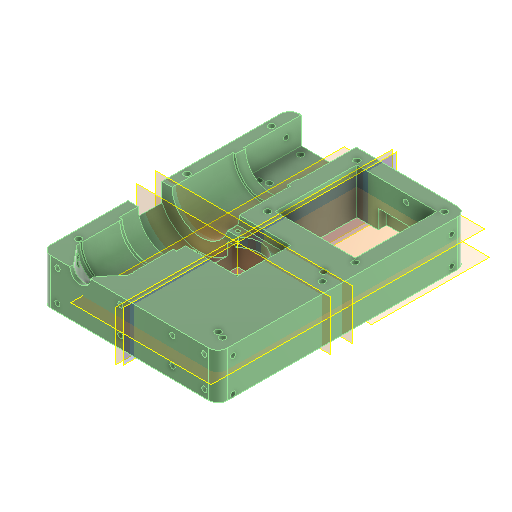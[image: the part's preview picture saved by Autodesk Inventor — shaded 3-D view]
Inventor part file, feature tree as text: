
AUTODESK INVENTOR PART (.ipt)
format: ipt  version: 2024.1 (Build 281209000, 209)  size: 665,600 bytes
history: native  units: mm
features: reference x15, sketch x10, plane x7, other x6, projected_geometry x6, extrude x5, hole x4, mirror x2, revolve x1, fillet x1
ambient origin geometry x8: Origin, YZ Plane, XZ Plane, XY Plane, X Axis, Y Axis, Z Axis, Center Point
bodies: Volumenkörper1 (feature_tree)
feature tree (57):
  plane  "Arbeitsebene1"
  plane  "Arbeitsebene2"
  extrude  "Extrusion1"  Depth=2.8mm
  revolve  "Umdrehung1"
  extrude  "Extrusion4"  Depth=2.8mm
  hole  "Bohrung1"  [1 undecoded]
  hole  "Bohrung2"  [1 undecoded]
  extrude  "Extrusion7"  TaperAngle=360.0deg  [1 undecoded]
  fillet  "Rundung2"  Radius=0.3mm
  hole  "Bohrung6"  [1 undecoded]
  other  "Arbeitsachse1"
  plane  "Arbeitsebene5"
  extrude  "Extrusion8"  Depth=31.15mm
  extrude  "Extrusion9"  Depth=1.0mm
  plane  "Arbeitsebene6"
  mirror  "Spiegeln1"
  plane  "Arbeitsebene7"
  mirror  "Spiegeln2"
  hole  "Bohrung7"  [1 undecoded]
  sketch  "Skizze1"  dims[d0=0.5mm d1=2.8mm]
  sketch  "Skizze2"  dims[d2=2.8mm d3=2.8mm]
  projected_geometry  "Projizierte Kontur1"
  sketch  "Skizze5"  dims[d4=2.8mm d5=95.0mm]
  projected_geometry  "Projizierte Kontur2"
  reference  "Referenz19"
  reference  "Referenz20"
  sketch  "Skizze6"  dims[d6=132.0mm d7=50.0mm d8=0.0mm]
  projected_geometry  "Projizierte Kontur3"
  sketch  "Skizze8"  dims[d9=0.25mm d10=360.0deg d23=0.3mm]
  projected_geometry  "Projizierte Kontur4"
  sketch  "Skizze13"  dims[d24=14.3mm d25=0.0mm d26=10.0mm]
  projected_geometry  "Projizierte Kontur8"
  sketch  "Skizze14"  dims[d27=3.3mm d28=6.0mm d29=4.0mm d30=8.0mm d31=90.0deg d32=8.0mm d33=20.594885mm d41=31.15mm]
  plane  "Arbeitsebene3"
  plane  "Arbeitsebene4"
  sketch  "Skizze15"  dims[d43=2.8mm d44=6.0mm d45=6.5mm d46=8.0mm d47=90.0deg d48=12.0mm d49=20.594885mm d74=1.0mm]
  reference  "Referenz28"
  reference  "Referenz29"
  reference  "Referenz30"
  reference  "Referenz31"
  reference  "Referenz32"
  reference  "Referenz33"
  projected_geometry  "Projizierte Kontur9"
  reference  "Referenz34"
  reference  "Referenz35"
  reference  "Referenz36"
  reference  "Referenz37"
  sketch  "Skizze16"  dims[d75=2.25mm d80=20.0mm]
  reference  "Referenz39"
  sketch  "Skizze17"  dims[d81=9.0mm d82=10.0mm d83=0.0mm d84=5.0mm d85=2.8mm d86=6.0mm d87=4.0mm d88=2.0mm d89=90.0deg d90=12.0mm d91=20.594885mm d92=28.5mm d93=28.5mm d96=-10.0mm d97=25.0mm d98=5.0mm d99=0.0mm d101=45.0mm d102=18.0mm d103=0.0mm d104=15.4mm d105=55.0mm d107=43.3mm d108=43.0mm d109=2.0mm d110=2.0mm d111=2.0mm d112=2.0mm d113=2.0mm d114=2.0mm d115=2.0mm d116=2.0mm d117=8.0mm d118=8.0mm d119=16.3mm d120=116.0mm d121=5.0mm d122=3.3mm d123=6.0mm d124=7.0mm d125=3.0mm d126=90.0deg d127=8.0mm d128=20.594885mm]
  reference  "Referenz40"
  reference  "Referenz41"
  other  "Assembly_Planktoscope_Uc2version_wormdrive_V3.iam"
  other  "00_HIKCamera_MV-CE060-10UMUC:1"
  other  "00_NEMA11:1"
  other  "00_10x_Objective_ViewSolutions_bm05073332:2"
  other  "00_NEMA17_Perestalticpump_Adapter:1"
note: 5 required parameter values undecoded (feature->parameter linkage not recoverable at this tier; creation-order binding heuristic only, values carry confidence <= 0.55)
